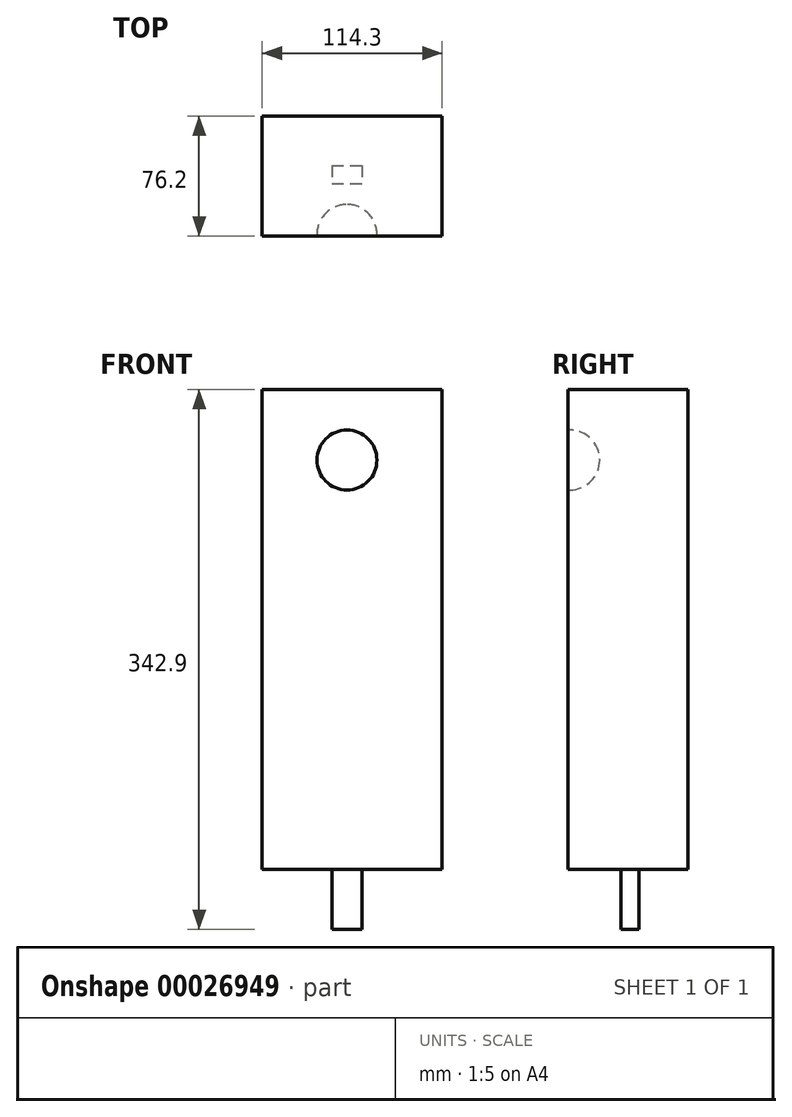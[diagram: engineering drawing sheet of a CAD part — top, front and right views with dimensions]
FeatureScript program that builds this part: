
annotation { "Feature Type Name" : "Feature", "Feature Type Description" : "" }
export const myFeature = defineFeature(function(context is Context, id is Id, definition is map)
    precondition{}
    {
        {
            var Q0;
            Q0=qCreatedBy(makeId("Top.planeOp"),FACE);
            var sketch = newSketch(context, id + "F0", { "sketchPlane" : qUnion([Q0])});
            skLineSegment(sketch, "E0.bottom", {"start": v(-9.53, 5.71) * mm, "end": v(9.52, 5.71) * mm});
            skLineSegment(sketch, "E0.top", {"start": v(-9.53, -5.72) * mm, "end": v(9.52, -5.71) * mm});
            skLineSegment(sketch, "E0.left", {"start": v(-9.53, 5.71) * mm, "end": v(-9.53, -5.72) * mm});
            skLineSegment(sketch, "E0.right", {"start": v(9.52, 5.71) * mm, "end": v(9.52, -5.72) * mm});
            skSolve(sketch);
        }
        {
            var Q0;
            Q0=makeQuery(id+"F0.imprint","IMPRINT",FACE,{"disambiguationData":[TD([[makeQuery(id+"F0.imprint","IMPRINT",EDGE,{"derivedFrom":sQuery(id+"F0.wireOp",EDGE,"E0.bottom")}),-1.0]])]});
            extrude(context, id + "F1", {"entities" : qUnion([Q0]), "depth" : 38.1 * mm});
        }
        {
            var Q0;
            Q0=qCreatedBy(makeId("Top.planeOp"),FACE);
            cPlane(context, id + "F2", {"entities" : qUnion([Q0]), "cplaneType" : CPlaneType.OFFSET, "offset" : 38.1 * mm, "width" : 152.4 * mm, "height" : 152.4 * mm});
        }
        {
            var Q0;
            Q0=qCreatedBy(id+"F2.planeOp",FACE);
            var sketch = newSketch(context, id + "F3", { "sketchPlane" : qUnion([Q0])});
            skLineSegment(sketch, "E1.bottom", {"start": v(-53.85, 37.06) * mm, "end": v(60.45, 37.06) * mm});
            skLineSegment(sketch, "E1.top", {"start": v(-53.85, -39.14) * mm, "end": v(60.45, -39.14) * mm});
            skLineSegment(sketch, "E1.left", {"start": v(-53.85, 37.06) * mm, "end": v(-53.85, -39.14) * mm});
            skLineSegment(sketch, "E1.right", {"start": v(60.45, 37.06) * mm, "end": v(60.45, -39.14) * mm});
            skSolve(sketch);
        }
        {
            var Q0;
            Q0=makeQuery(id+"F3.imprint","IMPRINT",FACE,{"disambiguationData":[TD([[makeQuery(id+"F3.imprint","IMPRINT",EDGE,{"derivedFrom":sQuery(id+"F3.wireOp",EDGE,"E1.bottom")}),-1.0]])]});
            extrude(context, id + "F4", {"entities" : qUnion([Q0]), "operationType" : NewBodyOperationType.ADD, "depth" : 304.8 * mm});
        }
        {
            var Q0;
            Q0=qCreatedBy(makeId("Front.planeOp"),FACE);
            cPlane(context, id + "F5", {"entities" : qUnion([Q0]), "cplaneType" : CPlaneType.OFFSET, "offset" : 38.1 * mm, "width" : 152.4 * mm, "height" : 152.4 * mm});
        }
        {
            var Q0;
            Q0=qCreatedBy(id+"F5.planeOp",FACE);
            var sketch = newSketch(context, id + "F6", { "sketchPlane" : qUnion([Q0])});
            skLineSegment(sketch, "E2", {"start": v(0, 317.18) * mm, "end": v(0, 279.08) * mm});
            skArc(sketch, "E3", {"start": v(0, 279.08) * mm, "mid": v(19.05, 298.13) * mm, "end": v(0, 317.18) * mm});
            skSolve(sketch);
        }
        {
            var Q0;
            Q0 = qSketchRegion(id + "F6", true);
            var Q1;
            Q1=sQuery(id+"F6.wireOp",EDGE,"E2");
            revolve(context, id + "F7", {"operationType" : NewBodyOperationType.REMOVE, "entities" : qUnion([Q0]), "axis" : qUnion([Q1]), "revolveType" : RevolveType.FULL, "oppositeDirection" : true});
        }
    });
